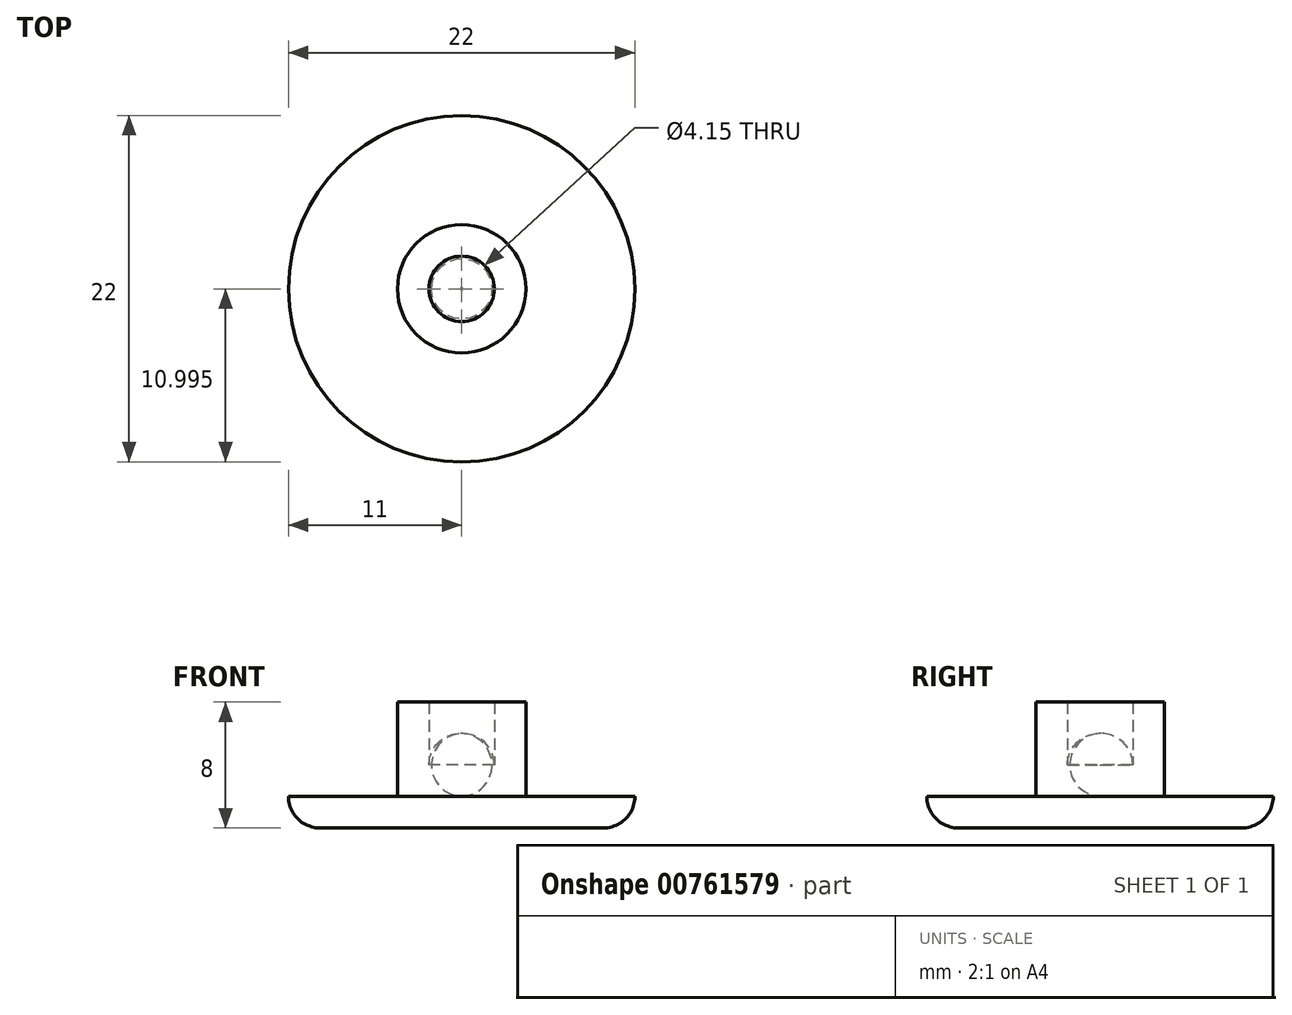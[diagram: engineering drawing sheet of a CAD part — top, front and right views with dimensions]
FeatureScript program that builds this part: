
annotation { "Feature Type Name" : "Feature", "Feature Type Description" : "" }
export const myFeature = defineFeature(function(context is Context, id is Id, definition is map)
    precondition{}
    {
        {
            var Q0;
            Q0=qCreatedBy(makeId("Top.planeOp"),FACE);
            var sketch = newSketch(context, id + "F0", { "sketchPlane" : qUnion([Q0])});
            skCircle(sketch, "E0", {"center": v(0, 21.97) * mm, "radius": 11 * mm});
            skSolve(sketch);
        }
        {
            var Q0;
            Q0 = qSketchRegion(id + "F0", true);
            extrude(context, id + "F1", {"entities" : qUnion([Q0]), "depth" : 2 * mm, "offsetDistance" : 25 * mm});
        }
        {
            var Q0;
            Q0=makeQuery(id+"F1.opExtrude","CAP_FACE",FACE,{"disambiguationData":[OSD([sQuery(id+"F0.wireOp",EDGE,"E0")])],"isStart":false});
            var sketch = newSketch(context, id + "F2", { "sketchPlane" : qUnion([Q0])});
            skSolve(sketch);
        }
        {
            var Q0;
            Q0=makeQuery(id+"F2.imprint","IMPRINT",FACE,{"disambiguationData":[TD([[makeQuery(id+"F2.imprint","IMPRINT",EDGE,{"derivedFrom":makeQuery(id+"F1.opExtrude","CAP_EDGE",EDGE,{"disambiguationData":[OSD([sQuery(id+"F0.wireOp",EDGE,"E0")])],"isStart":false})}),1.0]])]});
            var sketch = newSketch(context, id + "F3", { "sketchPlane" : qUnion([Q0])});
            skCircle(sketch, "E1", {"center": v(0, 21.97) * mm, "radius": 4.08 * mm});
            skCircle(sketch, "E2", {"center": v(0, 21.97) * mm, "radius": 2.08 * mm});
            skSolve(sketch);
        }
        {
            var Q0;
            Q0 = qSketchRegion(id + "F3", true);
            extrude(context, id + "F4", {"entities" : qUnion([Q0]), "operationType" : NewBodyOperationType.ADD, "depth" : 6 * mm, "offsetDistance" : 25 * mm});
        }
        {
            var Q0;
            Q0=makeQuery(id+"F4.opExtrude","CAP_EDGE",EDGE,{"disambiguationData":[OSD([sQuery(id+"F3.wireOp",EDGE,"4MA3MI5k-ulWB-dGuy-IlwO-mQeR1FPx0EC6")])],"isStart":true});
            var Q1;
            Q1=makeQuery(id+"F1.opExtrude","CAP_EDGE",EDGE,{"disambiguationData":[OSD([sQuery(id+"F0.wireOp",EDGE,"E0")])],"isStart":true});
            fillet(context, id + "F5", {"entities" : qUnion([Q0, Q1]), "radius" : 2 * mm, "tangentPropagation" : true, "allowEdgeOverflow" : false});
        }
        {
            var Q0;
            Q0=makeQuery(id+"F4.opExtrude","CAP_EDGE",EDGE,{"disambiguationData":[OSD([sQuery(id+"F3.wireOp",EDGE,"E2")])],"isStart":true});
            fillet(context, id + "F6", {"entities" : qUnion([Q0]), "radius" : 2 * mm, "tangentPropagation" : true, "allowEdgeOverflow" : false});
        }
    });
